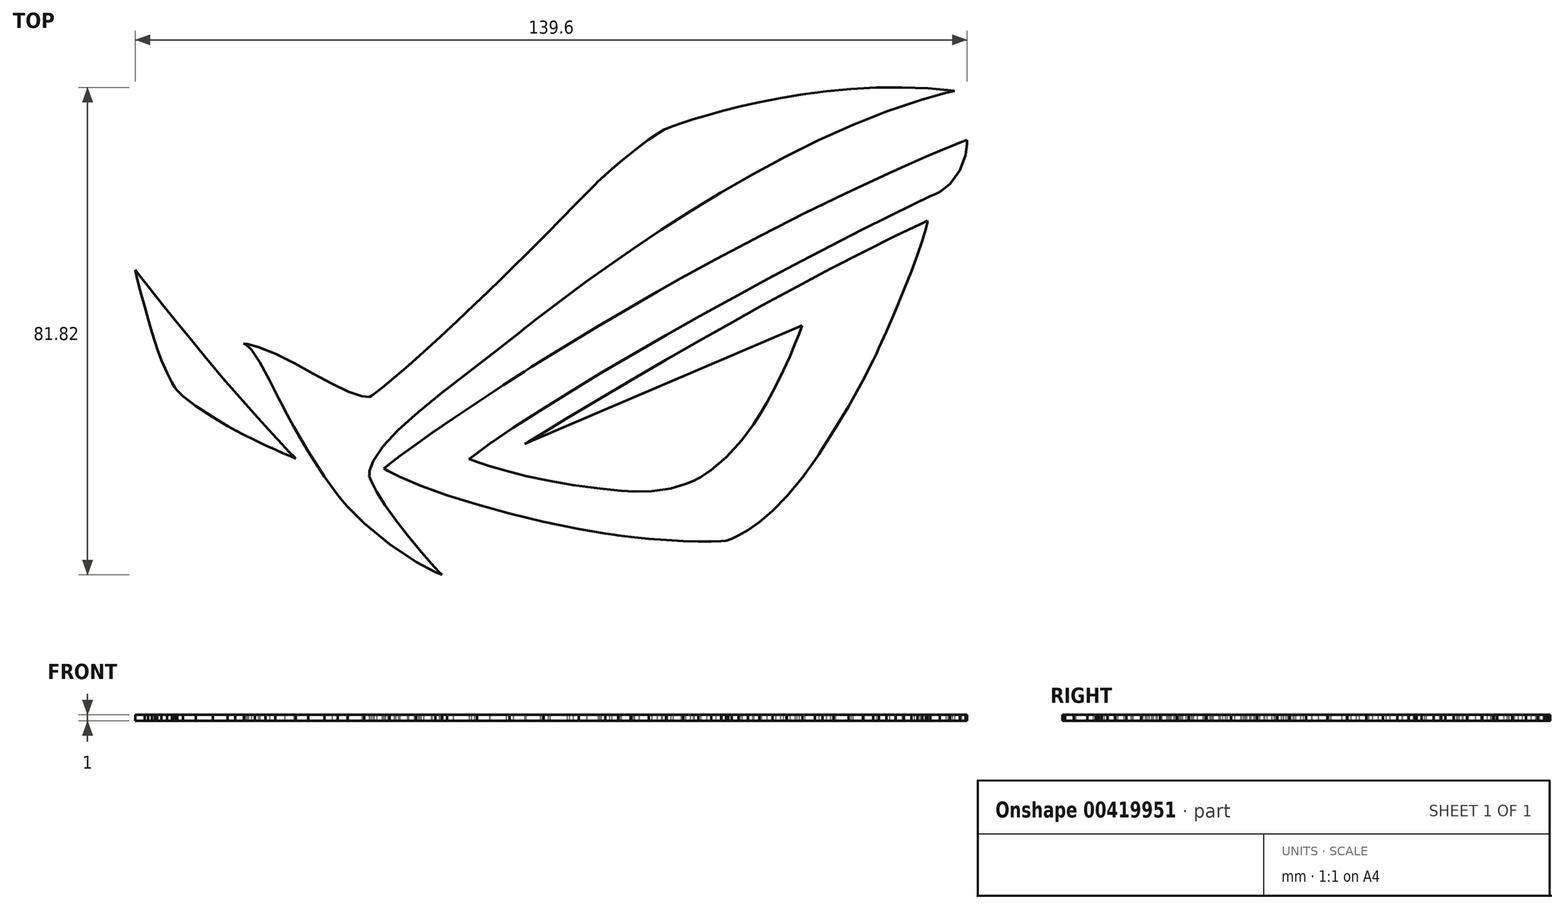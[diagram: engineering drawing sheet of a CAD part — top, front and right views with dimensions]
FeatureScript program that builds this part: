
annotation { "Feature Type Name" : "Feature", "Feature Type Description" : "" }
export const myFeature = defineFeature(function(context is Context, id is Id, definition is map)
    precondition{}
    {
        {
            var Q0;
            Q0=qCreatedBy(makeId("Top.planeOp"),FACE);
            var sketch = newSketch(context, id + "F0", { "sketchPlane" : qUnion([Q0])});
            skLineSegment(sketch, "E0", {"start": v(-3.34, -6.05) * mm, "end": v(-1.53, -4.9) * mm});
            skLineSegment(sketch, "E1", {"start": v(-1.53, -4.9) * mm, "end": v(7.85, 0.84) * mm});
            skLineSegment(sketch, "E2", {"start": v(7.85, 0.84) * mm, "end": v(17.77, 6.62) * mm});
            skLineSegment(sketch, "E3", {"start": v(17.77, 6.62) * mm, "end": v(19.86, 7.8) * mm});
            skLineSegment(sketch, "E4", {"start": v(19.86, 7.8) * mm, "end": v(21.8, 8.88) * mm});
            skLineSegment(sketch, "E5", {"start": v(21.8, 8.88) * mm, "end": v(27.63, 12.07) * mm});
            skLineSegment(sketch, "E6", {"start": v(27.63, 12.07) * mm, "end": v(35.25, 16.09) * mm});
            skLineSegment(sketch, "E7", {"start": v(35.25, 16.09) * mm, "end": v(42.56, 19.79) * mm});
            skLineSegment(sketch, "E8", {"start": v(42.56, 19.79) * mm, "end": v(47.68, 22.3) * mm});
            skLineSegment(sketch, "E9", {"start": v(47.68, 22.3) * mm, "end": v(49.4, 23.12) * mm});
            skLineSegment(sketch, "E10", {"start": v(49.4, 23.12) * mm, "end": v(50.35, 23.58) * mm});
            skLineSegment(sketch, "E11", {"start": v(50.35, 23.58) * mm, "end": v(53.22, 24.92) * mm});
            skLineSegment(sketch, "E12", {"start": v(53.22, 24.92) * mm, "end": v(56.76, 26.55) * mm});
            skLineSegment(sketch, "E13", {"start": v(56.76, 26.55) * mm, "end": v(59.99, 28) * mm});
            skLineSegment(sketch, "E14", {"start": v(59.99, 28) * mm, "end": v(62.85, 29.25) * mm});
            skLineSegment(sketch, "E15", {"start": v(62.85, 29.25) * mm, "end": v(65.3, 30.3) * mm});
            skLineSegment(sketch, "E16", {"start": v(65.3, 30.3) * mm, "end": v(67.3, 31.13) * mm});
            skLineSegment(sketch, "E17", {"start": v(67.3, 31.13) * mm, "end": v(68.82, 31.72) * mm});
            skLineSegment(sketch, "E18", {"start": v(68.82, 31.72) * mm, "end": v(69.54, 32) * mm});
            skLineSegment(sketch, "E19", {"start": v(69.54, 32) * mm, "end": v(69.79, 32.07) * mm});
            skLineSegment(sketch, "E20", {"start": v(69.79, 32.07) * mm, "end": v(69.8, 31.43) * mm});
            skLineSegment(sketch, "E21", {"start": v(69.8, 31.43) * mm, "end": v(69.52, 29.51) * mm});
            skLineSegment(sketch, "E22", {"start": v(69.52, 29.51) * mm, "end": v(68.57, 26.96) * mm});
            skLineSegment(sketch, "E23", {"start": v(68.57, 26.96) * mm, "end": v(66.93, 24.71) * mm});
            skLineSegment(sketch, "E24", {"start": v(66.93, 24.71) * mm, "end": v(65.21, 23.36) * mm});
            skLineSegment(sketch, "E25", {"start": v(65.21, 23.36) * mm, "end": v(64.57, 23.06) * mm});
            skLineSegment(sketch, "E26", {"start": v(64.57, 23.06) * mm, "end": v(63.65, 22.64) * mm});
            skLineSegment(sketch, "E27", {"start": v(63.65, 22.64) * mm, "end": v(60.91, 21.35) * mm});
            skLineSegment(sketch, "E28", {"start": v(60.91, 21.35) * mm, "end": v(56.74, 19.32) * mm});
            skLineSegment(sketch, "E29", {"start": v(56.74, 19.32) * mm, "end": v(52.11, 17) * mm});
            skLineSegment(sketch, "E30", {"start": v(52.11, 17) * mm, "end": v(47.11, 14.44) * mm});
            skLineSegment(sketch, "E31", {"start": v(47.11, 14.44) * mm, "end": v(41.82, 11.67) * mm});
            skLineSegment(sketch, "E32", {"start": v(41.82, 11.67) * mm, "end": v(36.31, 8.74) * mm});
            skLineSegment(sketch, "E33", {"start": v(36.31, 8.74) * mm, "end": v(30.67, 5.67) * mm});
            skLineSegment(sketch, "E34", {"start": v(30.67, 5.67) * mm, "end": v(24.95, 2.52) * mm});
            skLineSegment(sketch, "E35", {"start": v(24.95, 2.52) * mm, "end": v(19.26, -0.7) * mm});
            skLineSegment(sketch, "E36", {"start": v(19.26, -0.7) * mm, "end": v(13.65, -3.92) * mm});
            skLineSegment(sketch, "E37", {"start": v(13.65, -3.92) * mm, "end": v(8.21, -7.12) * mm});
            skLineSegment(sketch, "E38", {"start": v(8.21, -7.12) * mm, "end": v(3.02, -10.27) * mm});
            skLineSegment(sketch, "E39", {"start": v(3.02, -10.27) * mm, "end": v(-1.85, -13.31) * mm});
            skLineSegment(sketch, "E40", {"start": v(-1.85, -13.31) * mm, "end": v(-6.32, -16.22) * mm});
            skLineSegment(sketch, "E41", {"start": v(-6.32, -16.22) * mm, "end": v(-10.32, -18.95) * mm});
            skLineSegment(sketch, "E42", {"start": v(-10.32, -18.95) * mm, "end": v(-12.92, -20.82) * mm});
            skLineSegment(sketch, "E43", {"start": v(-12.92, -20.82) * mm, "end": v(-13.76, -21.47) * mm});
            skLineSegment(sketch, "E44", {"start": v(-13.76, -21.47) * mm, "end": v(-13.42, -21.61) * mm});
            skLineSegment(sketch, "E45", {"start": v(-13.42, -21.61) * mm, "end": v(-12.37, -22) * mm});
            skLineSegment(sketch, "E46", {"start": v(-12.37, -22) * mm, "end": v(-10.27, -22.68) * mm});
            skLineSegment(sketch, "E47", {"start": v(-10.27, -22.68) * mm, "end": v(-7.54, -23.46) * mm});
            skLineSegment(sketch, "E48", {"start": v(-7.54, -23.46) * mm, "end": v(-4.25, -24.3) * mm});
            skLineSegment(sketch, "E49", {"start": v(-4.25, -24.3) * mm, "end": v(-0.5, -25.1) * mm});
            skLineSegment(sketch, "E50", {"start": v(-0.5, -25.1) * mm, "end": v(3.68, -25.84) * mm});
            skLineSegment(sketch, "E51", {"start": v(3.68, -25.84) * mm, "end": v(8.17, -26.45) * mm});
            skLineSegment(sketch, "E52", {"start": v(8.17, -26.45) * mm, "end": v(11.73, -26.79) * mm});
            skLineSegment(sketch, "E53", {"start": v(11.73, -26.79) * mm, "end": v(12.91, -26.86) * mm});
            skLineSegment(sketch, "E54", {"start": v(12.91, -26.86) * mm, "end": v(13.9, -26.92) * mm});
            skLineSegment(sketch, "E55", {"start": v(13.9, -26.92) * mm, "end": v(16.92, -26.86) * mm});
            skLineSegment(sketch, "E56", {"start": v(16.92, -26.86) * mm, "end": v(20.08, -26.4) * mm});
            skLineSegment(sketch, "E57", {"start": v(20.08, -26.4) * mm, "end": v(22.54, -25.68) * mm});
            skLineSegment(sketch, "E58", {"start": v(22.54, -25.68) * mm, "end": v(23.97, -25.07) * mm});
            skLineSegment(sketch, "E59", {"start": v(23.97, -25.07) * mm, "end": v(24.44, -24.84) * mm});
            skLineSegment(sketch, "E60", {"start": v(24.44, -24.84) * mm, "end": v(25.07, -24.51) * mm});
            skLineSegment(sketch, "E61", {"start": v(25.07, -24.51) * mm, "end": v(26.86, -23.33) * mm});
            skLineSegment(sketch, "E62", {"start": v(26.86, -23.33) * mm, "end": v(29.4, -21.17) * mm});
            skLineSegment(sketch, "E63", {"start": v(29.4, -21.17) * mm, "end": v(31.99, -18.31) * mm});
            skLineSegment(sketch, "E64", {"start": v(31.99, -18.31) * mm, "end": v(33.98, -15.64) * mm});
            skLineSegment(sketch, "E65", {"start": v(33.98, -15.64) * mm, "end": v(34.57, -14.7) * mm});
            skLineSegment(sketch, "E66", {"start": v(34.57, -14.7) * mm, "end": v(35, -14.04) * mm});
            skLineSegment(sketch, "E67", {"start": v(35, -14.04) * mm, "end": v(36.2, -12) * mm});
            skLineSegment(sketch, "E68", {"start": v(36.2, -12) * mm, "end": v(37.66, -9.28) * mm});
            skLineSegment(sketch, "E69", {"start": v(37.66, -9.28) * mm, "end": v(38.94, -6.65) * mm});
            skLineSegment(sketch, "E70", {"start": v(38.94, -6.65) * mm, "end": v(40.04, -4.24) * mm});
            skLineSegment(sketch, "E71", {"start": v(40.04, -4.24) * mm, "end": v(40.91, -2.16) * mm});
            skLineSegment(sketch, "E72", {"start": v(40.91, -2.16) * mm, "end": v(41.56, -0.52) * mm});
            skLineSegment(sketch, "E73", {"start": v(41.56, -0.52) * mm, "end": v(41.97, 0.54) * mm});
            skLineSegment(sketch, "E74", {"start": v(41.97, 0.54) * mm, "end": v(42.1, 0.92) * mm});
            skLineSegment(sketch, "E75", {"start": v(42.1, 0.92) * mm, "end": v(-4.43, -18.94) * mm});
            skLineSegment(sketch, "E76", {"start": v(-4.43, -18.94) * mm, "end": v(-3.96, -18.66) * mm});
            skLineSegment(sketch, "E77", {"start": v(-3.96, -18.66) * mm, "end": v(-2.63, -17.84) * mm});
            skLineSegment(sketch, "E78", {"start": v(-2.63, -17.84) * mm, "end": v(-0.5, -16.54) * mm});
            skLineSegment(sketch, "E79", {"start": v(-0.5, -16.54) * mm, "end": v(2.34, -14.83) * mm});
            skLineSegment(sketch, "E80", {"start": v(2.34, -14.83) * mm, "end": v(5.8, -12.74) * mm});
            skLineSegment(sketch, "E81", {"start": v(5.8, -12.74) * mm, "end": v(9.84, -10.35) * mm});
            skLineSegment(sketch, "E82", {"start": v(9.84, -10.35) * mm, "end": v(14.34, -7.7) * mm});
            skLineSegment(sketch, "E83", {"start": v(14.34, -7.7) * mm, "end": v(19.23, -4.84) * mm});
            skLineSegment(sketch, "E84", {"start": v(19.23, -4.84) * mm, "end": v(24.45, -1.85) * mm});
            skLineSegment(sketch, "E85", {"start": v(24.45, -1.85) * mm, "end": v(29.9, 1.24) * mm});
            skLineSegment(sketch, "E86", {"start": v(29.9, 1.24) * mm, "end": v(35.5, 4.36) * mm});
            skLineSegment(sketch, "E87", {"start": v(35.5, 4.36) * mm, "end": v(41.2, 7.45) * mm});
            skLineSegment(sketch, "E88", {"start": v(41.2, 7.45) * mm, "end": v(46.88, 10.48) * mm});
            skLineSegment(sketch, "E89", {"start": v(46.88, 10.48) * mm, "end": v(52.49, 13.36) * mm});
            skLineSegment(sketch, "E90", {"start": v(52.49, 13.36) * mm, "end": v(57.93, 16.06) * mm});
            skLineSegment(sketch, "E91", {"start": v(57.93, 16.06) * mm, "end": v(61.83, 17.92) * mm});
            skLineSegment(sketch, "E92", {"start": v(61.83, 17.92) * mm, "end": v(63.14, 18.52) * mm});
            skLineSegment(sketch, "E93", {"start": v(63.14, 18.52) * mm, "end": v(63.09, 18.18) * mm});
            skLineSegment(sketch, "E94", {"start": v(63.09, 18.18) * mm, "end": v(62.84, 17.17) * mm});
            skLineSegment(sketch, "E95", {"start": v(62.84, 17.17) * mm, "end": v(62.27, 15.26) * mm});
            skLineSegment(sketch, "E96", {"start": v(62.27, 15.26) * mm, "end": v(61.46, 12.86) * mm});
            skLineSegment(sketch, "E97", {"start": v(61.46, 12.86) * mm, "end": v(60.43, 10.05) * mm});
            skLineSegment(sketch, "E98", {"start": v(60.43, 10.05) * mm, "end": v(59.2, 6.91) * mm});
            skLineSegment(sketch, "E99", {"start": v(59.2, 6.91) * mm, "end": v(57.8, 3.52) * mm});
            skLineSegment(sketch, "E100", {"start": v(57.8, 3.52) * mm, "end": v(56.26, -0.05) * mm});
            skLineSegment(sketch, "E101", {"start": v(56.26, -0.05) * mm, "end": v(55.02, -2.81) * mm});
            skLineSegment(sketch, "E102", {"start": v(55.02, -2.81) * mm, "end": v(54.6, -3.72) * mm});
            skLineSegment(sketch, "E103", {"start": v(54.6, -3.72) * mm, "end": v(54.06, -4.86) * mm});
            skLineSegment(sketch, "E104", {"start": v(54.06, -4.86) * mm, "end": v(52.34, -8.23) * mm});
            skLineSegment(sketch, "E105", {"start": v(52.34, -8.23) * mm, "end": v(49.9, -12.62) * mm});
            skLineSegment(sketch, "E106", {"start": v(49.9, -12.62) * mm, "end": v(47.39, -16.79) * mm});
            skLineSegment(sketch, "E107", {"start": v(47.39, -16.79) * mm, "end": v(45.55, -19.7) * mm});
            skLineSegment(sketch, "E108", {"start": v(45.55, -19.7) * mm, "end": v(44.93, -20.65) * mm});
            skLineSegment(sketch, "E109", {"start": v(44.93, -20.65) * mm, "end": v(44.28, -21.65) * mm});
            skLineSegment(sketch, "E110", {"start": v(44.28, -21.65) * mm, "end": v(42.18, -24.55) * mm});
            skLineSegment(sketch, "E111", {"start": v(42.18, -24.55) * mm, "end": v(39.56, -27.7) * mm});
            skLineSegment(sketch, "E112", {"start": v(39.56, -27.7) * mm, "end": v(37.12, -30.16) * mm});
            skLineSegment(sketch, "E113", {"start": v(37.12, -30.16) * mm, "end": v(34.92, -32.04) * mm});
            skLineSegment(sketch, "E114", {"start": v(34.92, -32.04) * mm, "end": v(33.01, -33.4) * mm});
            skLineSegment(sketch, "E115", {"start": v(33.01, -33.4) * mm, "end": v(31.45, -34.3) * mm});
            skLineSegment(sketch, "E116", {"start": v(31.45, -34.3) * mm, "end": v(30.28, -34.85) * mm});
            skLineSegment(sketch, "E117", {"start": v(30.28, -34.85) * mm, "end": v(29.75, -35.05) * mm});
            skLineSegment(sketch, "E118", {"start": v(29.75, -35.05) * mm, "end": v(29.57, -35.1) * mm});
            skLineSegment(sketch, "E119", {"start": v(29.57, -35.1) * mm, "end": v(29.31, -35.18) * mm});
            skLineSegment(sketch, "E120", {"start": v(29.31, -35.18) * mm, "end": v(28.51, -35.26) * mm});
            skLineSegment(sketch, "E121", {"start": v(28.51, -35.26) * mm, "end": v(26.84, -35.33) * mm});
            skLineSegment(sketch, "E122", {"start": v(26.84, -35.33) * mm, "end": v(24.68, -35.32) * mm});
            skLineSegment(sketch, "E123", {"start": v(24.68, -35.32) * mm, "end": v(22.13, -35.24) * mm});
            skLineSegment(sketch, "E124", {"start": v(22.13, -35.24) * mm, "end": v(19.33, -35.08) * mm});
            skLineSegment(sketch, "E125", {"start": v(19.33, -35.08) * mm, "end": v(16.38, -34.85) * mm});
            skLineSegment(sketch, "E126", {"start": v(16.38, -34.85) * mm, "end": v(13.41, -34.55) * mm});
            skLineSegment(sketch, "E127", {"start": v(13.41, -34.55) * mm, "end": v(11.26, -34.28) * mm});
            skLineSegment(sketch, "E128", {"start": v(11.26, -34.28) * mm, "end": v(10.54, -34.18) * mm});
            skLineSegment(sketch, "E129", {"start": v(10.54, -34.18) * mm, "end": v(9.06, -33.97) * mm});
            skLineSegment(sketch, "E130", {"start": v(9.06, -33.97) * mm, "end": v(4.66, -33.2) * mm});
            skLineSegment(sketch, "E131", {"start": v(4.66, -33.2) * mm, "end": v(-1.24, -32) * mm});
            skLineSegment(sketch, "E132", {"start": v(-1.24, -32) * mm, "end": v(-7, -30.6) * mm});
            skLineSegment(sketch, "E133", {"start": v(-7, -30.6) * mm, "end": v(-12.45, -29.1) * mm});
            skLineSegment(sketch, "E134", {"start": v(-12.45, -29.1) * mm, "end": v(-17.44, -27.54) * mm});
            skLineSegment(sketch, "E135", {"start": v(-17.44, -27.54) * mm, "end": v(-21.82, -25.98) * mm});
            skLineSegment(sketch, "E136", {"start": v(-21.82, -25.98) * mm, "end": v(-25.41, -24.46) * mm});
            skLineSegment(sketch, "E137", {"start": v(-25.41, -24.46) * mm, "end": v(-27.43, -23.46) * mm});
            skLineSegment(sketch, "E138", {"start": v(-27.43, -23.46) * mm, "end": v(-28.07, -23.07) * mm});
            skLineSegment(sketch, "E139", {"start": v(-28.07, -23.07) * mm, "end": v(-27.84, -22.85) * mm});
            skLineSegment(sketch, "E140", {"start": v(-27.84, -22.85) * mm, "end": v(-27.11, -22.27) * mm});
            skLineSegment(sketch, "E141", {"start": v(-27.11, -22.27) * mm, "end": v(-25.4, -20.97) * mm});
            skLineSegment(sketch, "E142", {"start": v(-25.4, -20.97) * mm, "end": v(-23, -19.23) * mm});
            skLineSegment(sketch, "E143", {"start": v(-23, -19.23) * mm, "end": v(-19.99, -17.1) * mm});
            skLineSegment(sketch, "E144", {"start": v(-19.99, -17.1) * mm, "end": v(-16.44, -14.67) * mm});
            skLineSegment(sketch, "E145", {"start": v(-16.44, -14.67) * mm, "end": v(-12.43, -11.97) * mm});
            skLineSegment(sketch, "E146", {"start": v(-12.43, -11.97) * mm, "end": v(-8.04, -9.08) * mm});
            skLineSegment(sketch, "E147", {"start": v(-8.04, -9.08) * mm, "end": v(-4.52, -6.8) * mm});
            skLineSegment(sketch, "E148", {"start": v(-4.52, -6.8) * mm, "end": v(-3.34, -6.05) * mm});
            skLineSegment(sketch, "E149", {"start": v(-53.46, -16.39) * mm, "end": v(-54.3, -15.93) * mm});
            skLineSegment(sketch, "E150", {"start": v(-54.3, -15.93) * mm, "end": v(-56.8, -14.44) * mm});
            skLineSegment(sketch, "E151", {"start": v(-56.8, -14.44) * mm, "end": v(-59.64, -12.56) * mm});
            skLineSegment(sketch, "E152", {"start": v(-59.64, -12.56) * mm, "end": v(-61.78, -10.9) * mm});
            skLineSegment(sketch, "E153", {"start": v(-61.78, -10.9) * mm, "end": v(-62.76, -10) * mm});
            skLineSegment(sketch, "E154", {"start": v(-62.76, -10) * mm, "end": v(-62.99, -9.68) * mm});
            skLineSegment(sketch, "E155", {"start": v(-62.99, -9.68) * mm, "end": v(-63.17, -9.43) * mm});
            skLineSegment(sketch, "E156", {"start": v(-63.17, -9.43) * mm, "end": v(-63.65, -8.61) * mm});
            skLineSegment(sketch, "E157", {"start": v(-63.65, -8.61) * mm, "end": v(-64.47, -6.99) * mm});
            skLineSegment(sketch, "E158", {"start": v(-64.47, -6.99) * mm, "end": v(-65.4, -4.87) * mm});
            skLineSegment(sketch, "E159", {"start": v(-65.4, -4.87) * mm, "end": v(-66.1, -2.96) * mm});
            skLineSegment(sketch, "E160", {"start": v(-66.1, -2.96) * mm, "end": v(-66.32, -2.32) * mm});
            skLineSegment(sketch, "E161", {"start": v(-66.32, -2.32) * mm, "end": v(-66.5, -1.78) * mm});
            skLineSegment(sketch, "E162", {"start": v(-66.5, -1.78) * mm, "end": v(-67, -0.17) * mm});
            skLineSegment(sketch, "E163", {"start": v(-67, -0.17) * mm, "end": v(-67.64, 2) * mm});
            skLineSegment(sketch, "E164", {"start": v(-67.64, 2) * mm, "end": v(-68.23, 4.12) * mm});
            skLineSegment(sketch, "E165", {"start": v(-68.23, 4.12) * mm, "end": v(-68.75, 6.07) * mm});
            skLineSegment(sketch, "E166", {"start": v(-68.75, 6.07) * mm, "end": v(-69.19, 7.76) * mm});
            skLineSegment(sketch, "E167", {"start": v(-69.19, 7.76) * mm, "end": v(-69.52, 9.09) * mm});
            skLineSegment(sketch, "E168", {"start": v(-69.52, 9.09) * mm, "end": v(-69.73, 9.96) * mm});
            skLineSegment(sketch, "E169", {"start": v(-69.73, 9.96) * mm, "end": v(-69.8, 10.27) * mm});
            skLineSegment(sketch, "E170", {"start": v(-69.8, 10.27) * mm, "end": v(-69.47, 9.84) * mm});
            skLineSegment(sketch, "E171", {"start": v(-69.47, 9.84) * mm, "end": v(-68.52, 8.64) * mm});
            skLineSegment(sketch, "E172", {"start": v(-68.52, 8.64) * mm, "end": v(-67.08, 6.8) * mm});
            skLineSegment(sketch, "E173", {"start": v(-67.08, 6.8) * mm, "end": v(-65.22, 4.46) * mm});
            skLineSegment(sketch, "E174", {"start": v(-65.22, 4.46) * mm, "end": v(-63.05, 1.76) * mm});
            skLineSegment(sketch, "E175", {"start": v(-63.05, 1.76) * mm, "end": v(-60.67, -1.17) * mm});
            skLineSegment(sketch, "E176", {"start": v(-60.67, -1.17) * mm, "end": v(-58.18, -4.2) * mm});
            skLineSegment(sketch, "E177", {"start": v(-58.18, -4.2) * mm, "end": v(-56.3, -6.43) * mm});
            skLineSegment(sketch, "E178", {"start": v(-56.3, -6.43) * mm, "end": v(-55.67, -7.17) * mm});
            skLineSegment(sketch, "E179", {"start": v(-55.67, -7.17) * mm, "end": v(-55.05, -7.9) * mm});
            skLineSegment(sketch, "E180", {"start": v(-55.05, -7.9) * mm, "end": v(-53.16, -10.1) * mm});
            skLineSegment(sketch, "E181", {"start": v(-53.16, -10.1) * mm, "end": v(-50.79, -12.79) * mm});
            skLineSegment(sketch, "E182", {"start": v(-50.79, -12.79) * mm, "end": v(-48.62, -15.2) * mm});
            skLineSegment(sketch, "E183", {"start": v(-48.62, -15.2) * mm, "end": v(-46.7, -17.3) * mm});
            skLineSegment(sketch, "E184", {"start": v(-46.7, -17.3) * mm, "end": v(-45.12, -19) * mm});
            skLineSegment(sketch, "E185", {"start": v(-45.12, -19) * mm, "end": v(-43.91, -20.3) * mm});
            skLineSegment(sketch, "E186", {"start": v(-43.91, -20.3) * mm, "end": v(-43.15, -21.1) * mm});
            skLineSegment(sketch, "E187", {"start": v(-43.15, -21.1) * mm, "end": v(-42.88, -21.38) * mm});
            skLineSegment(sketch, "E188", {"start": v(-42.88, -21.38) * mm, "end": v(-43.13, -21.28) * mm});
            skLineSegment(sketch, "E189", {"start": v(-43.13, -21.28) * mm, "end": v(-43.84, -20.98) * mm});
            skLineSegment(sketch, "E190", {"start": v(-43.84, -20.98) * mm, "end": v(-44.93, -20.5) * mm});
            skLineSegment(sketch, "E191", {"start": v(-44.93, -20.5) * mm, "end": v(-46.32, -19.9) * mm});
            skLineSegment(sketch, "E192", {"start": v(-46.32, -19.9) * mm, "end": v(-47.95, -19.15) * mm});
            skLineSegment(sketch, "E193", {"start": v(-47.95, -19.15) * mm, "end": v(-49.73, -18.3) * mm});
            skLineSegment(sketch, "E194", {"start": v(-49.73, -18.3) * mm, "end": v(-51.6, -17.37) * mm});
            skLineSegment(sketch, "E195", {"start": v(-51.6, -17.37) * mm, "end": v(-53, -16.64) * mm});
            skLineSegment(sketch, "E196", {"start": v(-53, -16.64) * mm, "end": v(-53.46, -16.39) * mm});
            skLineSegment(sketch, "E197", {"start": v(-4.17, 0.67) * mm, "end": v(-5.41, -0.3) * mm});
            skLineSegment(sketch, "E198", {"start": v(-5.41, -0.3) * mm, "end": v(-9.15, -3.21) * mm});
            skLineSegment(sketch, "E199", {"start": v(-9.15, -3.21) * mm, "end": v(-13.93, -6.9) * mm});
            skLineSegment(sketch, "E200", {"start": v(-13.93, -6.9) * mm, "end": v(-18.36, -10.35) * mm});
            skLineSegment(sketch, "E201", {"start": v(-18.36, -10.35) * mm, "end": v(-22.3, -13.59) * mm});
            skLineSegment(sketch, "E202", {"start": v(-22.3, -13.59) * mm, "end": v(-25.63, -16.58) * mm});
            skLineSegment(sketch, "E203", {"start": v(-25.63, -16.58) * mm, "end": v(-28.2, -19.32) * mm});
            skLineSegment(sketch, "E204", {"start": v(-28.2, -19.32) * mm, "end": v(-29.87, -21.8) * mm});
            skLineSegment(sketch, "E205", {"start": v(-29.87, -21.8) * mm, "end": v(-30.49, -23.44) * mm});
            skLineSegment(sketch, "E206", {"start": v(-30.49, -23.44) * mm, "end": v(-30.5, -24) * mm});
            skLineSegment(sketch, "E207", {"start": v(-30.5, -24) * mm, "end": v(-30.52, -24.3) * mm});
            skLineSegment(sketch, "E208", {"start": v(-30.52, -24.3) * mm, "end": v(-30.2, -25.21) * mm});
            skLineSegment(sketch, "E209", {"start": v(-30.2, -25.21) * mm, "end": v(-29.26, -27) * mm});
            skLineSegment(sketch, "E210", {"start": v(-29.26, -27) * mm, "end": v(-27.86, -29.21) * mm});
            skLineSegment(sketch, "E211", {"start": v(-27.86, -29.21) * mm, "end": v(-26.1, -31.67) * mm});
            skLineSegment(sketch, "E212", {"start": v(-26.1, -31.67) * mm, "end": v(-24.15, -34.23) * mm});
            skLineSegment(sketch, "E213", {"start": v(-24.15, -34.23) * mm, "end": v(-22.1, -36.73) * mm});
            skLineSegment(sketch, "E214", {"start": v(-22.1, -36.73) * mm, "end": v(-20.11, -39) * mm});
            skLineSegment(sketch, "E215", {"start": v(-20.11, -39) * mm, "end": v(-18.77, -40.45) * mm});
            skLineSegment(sketch, "E216", {"start": v(-18.77, -40.45) * mm, "end": v(-18.3, -40.91) * mm});
            skLineSegment(sketch, "E217", {"start": v(-18.3, -40.91) * mm, "end": v(-19.44, -40.45) * mm});
            skLineSegment(sketch, "E218", {"start": v(-19.44, -40.45) * mm, "end": v(-22.69, -38.73) * mm});
            skLineSegment(sketch, "E219", {"start": v(-22.69, -38.73) * mm, "end": v(-27.13, -35.78) * mm});
            skLineSegment(sketch, "E220", {"start": v(-27.13, -35.78) * mm, "end": v(-31.35, -32.27) * mm});
            skLineSegment(sketch, "E221", {"start": v(-31.35, -32.27) * mm, "end": v(-34.17, -29.45) * mm});
            skLineSegment(sketch, "E222", {"start": v(-34.17, -29.45) * mm, "end": v(-35.02, -28.43) * mm});
            skLineSegment(sketch, "E223", {"start": v(-35.02, -28.43) * mm, "end": v(-35.83, -27.47) * mm});
            skLineSegment(sketch, "E224", {"start": v(-35.83, -27.47) * mm, "end": v(-38.06, -24.43) * mm});
            skLineSegment(sketch, "E225", {"start": v(-38.06, -24.43) * mm, "end": v(-40.78, -20.21) * mm});
            skLineSegment(sketch, "E226", {"start": v(-40.78, -20.21) * mm, "end": v(-43.16, -16.08) * mm});
            skLineSegment(sketch, "E227", {"start": v(-43.16, -16.08) * mm, "end": v(-44.67, -13.28) * mm});
            skLineSegment(sketch, "E228", {"start": v(-44.67, -13.28) * mm, "end": v(-45.16, -12.34) * mm});
            skLineSegment(sketch, "E229", {"start": v(-45.16, -12.34) * mm, "end": v(-45.7, -11.33) * mm});
            skLineSegment(sketch, "E230", {"start": v(-45.7, -11.33) * mm, "end": v(-47.25, -8.27) * mm});
            skLineSegment(sketch, "E231", {"start": v(-47.25, -8.27) * mm, "end": v(-48.9, -5.2) * mm});
            skLineSegment(sketch, "E232", {"start": v(-48.9, -5.2) * mm, "end": v(-50.28, -3.13) * mm});
            skLineSegment(sketch, "E233", {"start": v(-50.28, -3.13) * mm, "end": v(-51.25, -2.24) * mm});
            skLineSegment(sketch, "E234", {"start": v(-51.25, -2.24) * mm, "end": v(-51.63, -2.1) * mm});
            skLineSegment(sketch, "E235", {"start": v(-51.63, -2.1) * mm, "end": v(-51, -2.14) * mm});
            skLineSegment(sketch, "E236", {"start": v(-51, -2.14) * mm, "end": v(-49.14, -2.64) * mm});
            skLineSegment(sketch, "E237", {"start": v(-49.14, -2.64) * mm, "end": v(-46.23, -3.82) * mm});
            skLineSegment(sketch, "E238", {"start": v(-46.23, -3.82) * mm, "end": v(-43.07, -5.42) * mm});
            skLineSegment(sketch, "E239", {"start": v(-43.07, -5.42) * mm, "end": v(-39.86, -7.17) * mm});
            skLineSegment(sketch, "E240", {"start": v(-39.86, -7.17) * mm, "end": v(-36.78, -8.84) * mm});
            skLineSegment(sketch, "E241", {"start": v(-36.78, -8.84) * mm, "end": v(-34, -10.18) * mm});
            skLineSegment(sketch, "E242", {"start": v(-34, -10.18) * mm, "end": v(-31.75, -10.93) * mm});
            skLineSegment(sketch, "E243", {"start": v(-31.75, -10.93) * mm, "end": v(-30.5, -11.02) * mm});
            skLineSegment(sketch, "E244", {"start": v(-30.5, -11.02) * mm, "end": v(-30.17, -10.86) * mm});
            skLineSegment(sketch, "E245", {"start": v(-30.17, -10.86) * mm, "end": v(-29.72, -10.54) * mm});
            skLineSegment(sketch, "E246", {"start": v(-29.72, -10.54) * mm, "end": v(-28.42, -9.53) * mm});
            skLineSegment(sketch, "E247", {"start": v(-28.42, -9.53) * mm, "end": v(-26.33, -7.82) * mm});
            skLineSegment(sketch, "E248", {"start": v(-26.33, -7.82) * mm, "end": v(-23.96, -5.79) * mm});
            skLineSegment(sketch, "E249", {"start": v(-23.96, -5.79) * mm, "end": v(-21.38, -3.48) * mm});
            skLineSegment(sketch, "E250", {"start": v(-21.38, -3.48) * mm, "end": v(-18.62, -0.97) * mm});
            skLineSegment(sketch, "E251", {"start": v(-18.62, -0.97) * mm, "end": v(-15.76, 1.7) * mm});
            skLineSegment(sketch, "E252", {"start": v(-15.76, 1.7) * mm, "end": v(-12.83, 4.5) * mm});
            skLineSegment(sketch, "E253", {"start": v(-12.83, 4.5) * mm, "end": v(-10.62, 6.61) * mm});
            skLineSegment(sketch, "E254", {"start": v(-10.62, 6.61) * mm, "end": v(-9.9, 7.32) * mm});
            skLineSegment(sketch, "E255", {"start": v(-9.9, 7.32) * mm, "end": v(-9.1, 8.1) * mm});
            skLineSegment(sketch, "E256", {"start": v(-9.1, 8.1) * mm, "end": v(-6.73, 10.42) * mm});
            skLineSegment(sketch, "E257", {"start": v(-6.73, 10.42) * mm, "end": v(-3.7, 13.43) * mm});
            skLineSegment(sketch, "E258", {"start": v(-3.7, 13.43) * mm, "end": v(-0.85, 16.28) * mm});
            skLineSegment(sketch, "E259", {"start": v(-0.85, 16.28) * mm, "end": v(1.74, 18.89) * mm});
            skLineSegment(sketch, "E260", {"start": v(1.74, 18.89) * mm, "end": v(4, 21.19) * mm});
            skLineSegment(sketch, "E261", {"start": v(4, 21.19) * mm, "end": v(5.88, 23.1) * mm});
            skLineSegment(sketch, "E262", {"start": v(5.88, 23.1) * mm, "end": v(7.3, 24.53) * mm});
            skLineSegment(sketch, "E263", {"start": v(7.3, 24.53) * mm, "end": v(7.97, 25.2) * mm});
            skLineSegment(sketch, "E264", {"start": v(7.97, 25.2) * mm, "end": v(8.2, 25.42) * mm});
            skLineSegment(sketch, "E265", {"start": v(8.2, 25.42) * mm, "end": v(8.4, 25.61) * mm});
            skLineSegment(sketch, "E266", {"start": v(8.4, 25.61) * mm, "end": v(9, 26.16) * mm});
            skLineSegment(sketch, "E267", {"start": v(9, 26.16) * mm, "end": v(10.15, 27.17) * mm});
            skLineSegment(sketch, "E268", {"start": v(10.15, 27.17) * mm, "end": v(11.56, 28.36) * mm});
            skLineSegment(sketch, "E269", {"start": v(11.56, 28.36) * mm, "end": v(13.13, 29.65) * mm});
            skLineSegment(sketch, "E270", {"start": v(13.13, 29.65) * mm, "end": v(14.76, 30.93) * mm});
            skLineSegment(sketch, "E271", {"start": v(14.76, 30.93) * mm, "end": v(16.34, 32.1) * mm});
            skLineSegment(sketch, "E272", {"start": v(16.34, 32.1) * mm, "end": v(17.78, 33.1) * mm});
            skLineSegment(sketch, "E273", {"start": v(17.78, 33.1) * mm, "end": v(18.67, 33.66) * mm});
            skLineSegment(sketch, "E274", {"start": v(18.67, 33.66) * mm, "end": v(18.97, 33.82) * mm});
            skLineSegment(sketch, "E275", {"start": v(18.97, 33.82) * mm, "end": v(19.1, 33.88) * mm});
            skLineSegment(sketch, "E276", {"start": v(19.1, 33.88) * mm, "end": v(19.48, 34.03) * mm});
            skLineSegment(sketch, "E277", {"start": v(19.48, 34.03) * mm, "end": v(20.47, 34.41) * mm});
            skLineSegment(sketch, "E278", {"start": v(20.47, 34.41) * mm, "end": v(21.93, 34.92) * mm});
            skLineSegment(sketch, "E279", {"start": v(21.93, 34.92) * mm, "end": v(23.81, 35.53) * mm});
            skLineSegment(sketch, "E280", {"start": v(23.81, 35.53) * mm, "end": v(26.09, 36.22) * mm});
            skLineSegment(sketch, "E281", {"start": v(26.09, 36.22) * mm, "end": v(28.72, 36.95) * mm});
            skLineSegment(sketch, "E282", {"start": v(28.72, 36.95) * mm, "end": v(31.7, 37.7) * mm});
            skLineSegment(sketch, "E283", {"start": v(31.7, 37.7) * mm, "end": v(34.95, 38.43) * mm});
            skLineSegment(sketch, "E284", {"start": v(34.95, 38.43) * mm, "end": v(38.47, 39.12) * mm});
            skLineSegment(sketch, "E285", {"start": v(38.47, 39.12) * mm, "end": v(42.23, 39.73) * mm});
            skLineSegment(sketch, "E286", {"start": v(42.23, 39.73) * mm, "end": v(46.17, 40.25) * mm});
            skLineSegment(sketch, "E287", {"start": v(46.17, 40.25) * mm, "end": v(50.28, 40.64) * mm});
            skLineSegment(sketch, "E288", {"start": v(50.28, 40.64) * mm, "end": v(54.52, 40.87) * mm});
            skLineSegment(sketch, "E289", {"start": v(54.52, 40.87) * mm, "end": v(58.86, 40.91) * mm});
            skLineSegment(sketch, "E290", {"start": v(58.86, 40.91) * mm, "end": v(63.25, 40.74) * mm});
            skLineSegment(sketch, "E291", {"start": v(63.25, 40.74) * mm, "end": v(66.58, 40.46) * mm});
            skLineSegment(sketch, "E292", {"start": v(66.58, 40.46) * mm, "end": v(67.68, 40.32) * mm});
            skLineSegment(sketch, "E293", {"start": v(67.68, 40.32) * mm, "end": v(66.26, 40) * mm});
            skLineSegment(sketch, "E294", {"start": v(66.26, 40) * mm, "end": v(62.04, 38.8) * mm});
            skLineSegment(sketch, "E295", {"start": v(62.04, 38.8) * mm, "end": v(56.32, 36.88) * mm});
            skLineSegment(sketch, "E296", {"start": v(56.32, 36.88) * mm, "end": v(50.6, 34.6) * mm});
            skLineSegment(sketch, "E297", {"start": v(50.6, 34.6) * mm, "end": v(44.9, 32.04) * mm});
            skLineSegment(sketch, "E298", {"start": v(44.9, 32.04) * mm, "end": v(39.28, 29.25) * mm});
            skLineSegment(sketch, "E299", {"start": v(39.28, 29.25) * mm, "end": v(33.78, 26.29) * mm});
            skLineSegment(sketch, "E300", {"start": v(33.78, 26.29) * mm, "end": v(28.45, 23.22) * mm});
            skLineSegment(sketch, "E301", {"start": v(28.45, 23.22) * mm, "end": v(23.34, 20.1) * mm});
            skLineSegment(sketch, "E302", {"start": v(23.34, 20.1) * mm, "end": v(18.49, 17) * mm});
            skLineSegment(sketch, "E303", {"start": v(18.49, 17) * mm, "end": v(13.95, 13.98) * mm});
            skLineSegment(sketch, "E304", {"start": v(13.95, 13.98) * mm, "end": v(9.76, 11.08) * mm});
            skLineSegment(sketch, "E305", {"start": v(9.76, 11.08) * mm, "end": v(5.98, 8.37) * mm});
            skLineSegment(sketch, "E306", {"start": v(5.98, 8.37) * mm, "end": v(2.65, 5.92) * mm});
            skLineSegment(sketch, "E307", {"start": v(2.65, 5.92) * mm, "end": v(-0.18, 3.78) * mm});
            skLineSegment(sketch, "E308", {"start": v(-0.18, 3.78) * mm, "end": v(-2.47, 2) * mm});
            skLineSegment(sketch, "E309", {"start": v(-2.47, 2) * mm, "end": v(-3.75, 1) * mm});
            skLineSegment(sketch, "E310", {"start": v(-3.75, 1) * mm, "end": v(-4.17, 0.67) * mm});
            skSolve(sketch);
        }
        {
            var Q0;
            Q0=makeQuery(id+"F0.imprint","IMPRINT",FACE,{"disambiguationData":[TD([[makeQuery(id+"F0.imprint","IMPRINT",EDGE,{"derivedFrom":sQuery(id+"F0.wireOp",EDGE,"E149")}),-1.0]])]});
            var Q1;
            Q1=makeQuery(id+"F0.imprint","IMPRINT",FACE,{"disambiguationData":[TD([[makeQuery(id+"F0.imprint","IMPRINT",EDGE,{"derivedFrom":sQuery(id+"F0.wireOp",EDGE,"E197")}),-1.0]])]});
            var Q2;
            Q2=makeQuery(id+"F0.imprint","IMPRINT",FACE,{"disambiguationData":[TD([[makeQuery(id+"F0.imprint","IMPRINT",EDGE,{"derivedFrom":sQuery(id+"F0.wireOp",EDGE,"E0")}),-1.0]])]});
            extrude(context, id + "F1", {"entities" : qUnion([Q0, Q1, Q2]), "depth" : 1 * mm});
        }
    });
